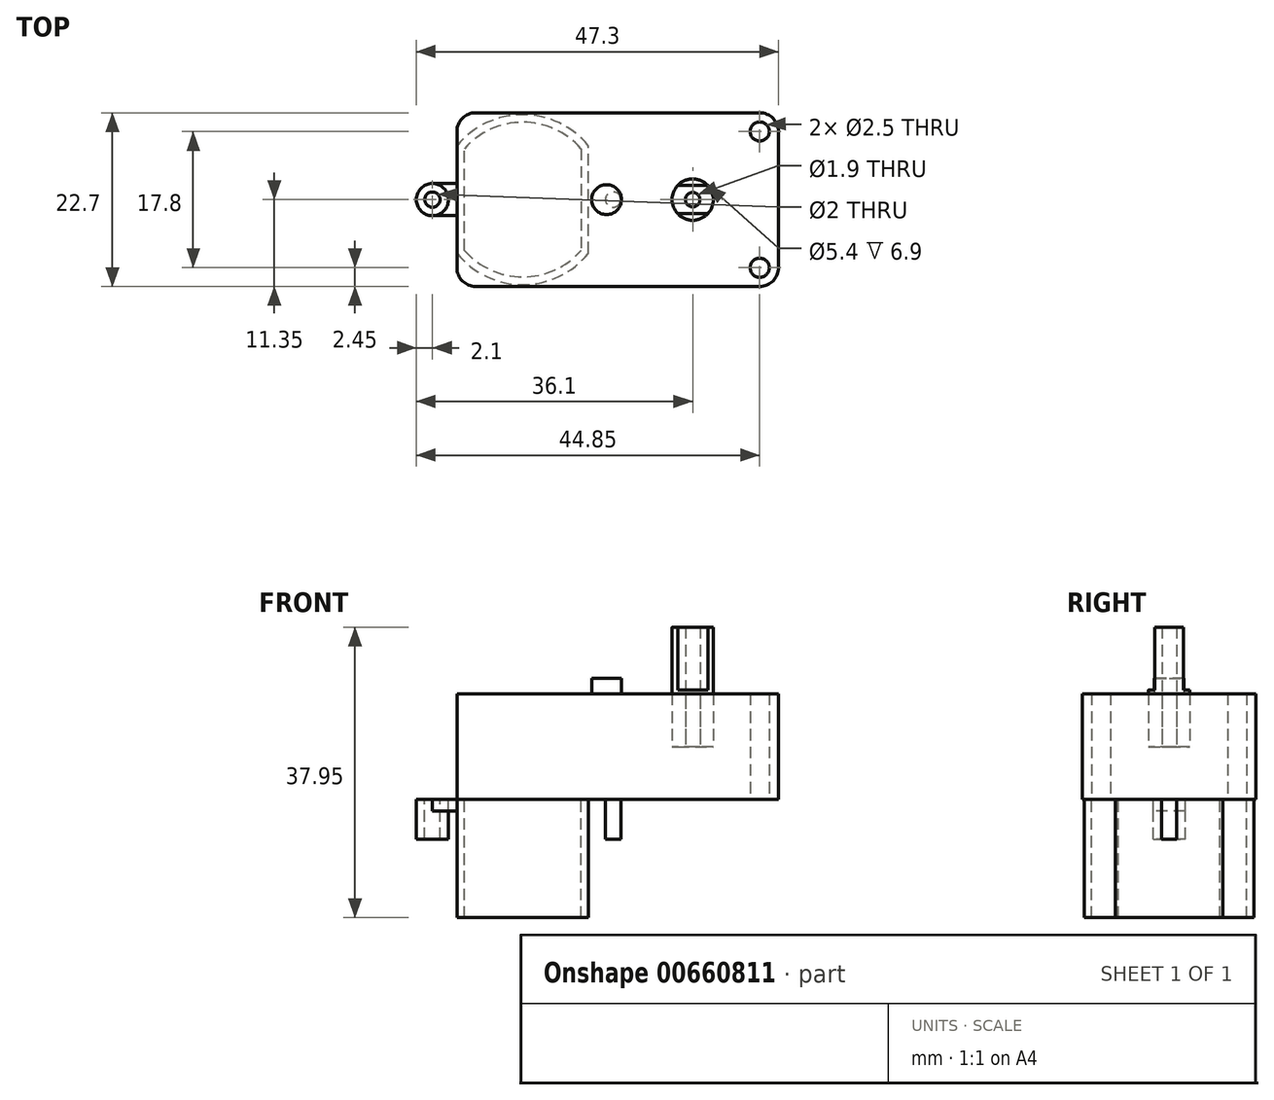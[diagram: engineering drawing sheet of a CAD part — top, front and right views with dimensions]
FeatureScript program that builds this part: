
annotation { "Feature Type Name" : "Feature", "Feature Type Description" : "" }
export const myFeature = defineFeature(function(context is Context, id is Id, definition is map)
    precondition{}
    {
        {
            var Q0;
            Q0=qCreatedBy(makeId("Top.planeOp"),FACE);
            var sketch = newSketch(context, id + "F0", { "sketchPlane" : qUnion([Q0])});
            skLineSegment(sketch, "E0.bottom", {"start": v(18.55, 11.35) * mm, "end": v(-18.55, 11.35) * mm});
            skLineSegment(sketch, "E0.top", {"start": v(18.55, -11.35) * mm, "end": v(-18.55, -11.35) * mm});
            skLineSegment(sketch, "E0.left", {"start": v(21, 8.9) * mm, "end": v(21, -8.9) * mm});
            skLineSegment(sketch, "E0.right", {"start": v(-21, 8.9) * mm, "end": v(-21, -8.9) * mm});
            skPoint(sketch, "E0.middle", {"position": v(0, 0) * mm});
            skLineSegment(sketch, "E1", {"start": v(-36.76, 0) * mm, "end": v(56.4, 0) * mm, "construction": true});
            skCircle(sketch, "E2", {"center": v(9.8, 0) * mm, "radius": 2.7 * mm});
            skPoint(sketch, "E3.visualSharp", {"position": v(21, 11.35) * mm});
            skArc(sketch, "E3.filletArc", {"start": v(21, 8.9) * mm, "mid": v(20.28, 10.63) * mm, "end": v(18.55, 11.35) * mm});
            skPoint(sketch, "E4.visualSharp", {"position": v(21, -11.35) * mm});
            skArc(sketch, "E4.filletArc", {"start": v(18.55, -11.35) * mm, "mid": v(20.28, -10.63) * mm, "end": v(21, -8.9) * mm});
            skPoint(sketch, "E5.visualSharp", {"position": v(-21, -11.35) * mm});
            skArc(sketch, "E5.filletArc", {"start": v(-21, -8.9) * mm, "mid": v(-20.28, -10.63) * mm, "end": v(-18.55, -11.35) * mm});
            skPoint(sketch, "E6.visualSharp", {"position": v(-21, 11.35) * mm});
            skArc(sketch, "E6.filletArc", {"start": v(-18.55, 11.35) * mm, "mid": v(-20.28, 10.63) * mm, "end": v(-21, 8.9) * mm});
            skCircle(sketch, "E7", {"center": v(18.55, 8.9) * mm, "radius": 1.25 * mm});
            skCircle(sketch, "E8", {"center": v(18.55, -8.9) * mm, "radius": 1.25 * mm});
            skCircle(sketch, "E9", {"center": v(9.8, 0) * mm, "radius": 0.95 * mm});
            skSolve(sketch);
        }
        {
            var Q0;
            Q0=makeQuery(id+"F0.imprint","IMPRINT",FACE,{"disambiguationData":[TD([[makeQuery(id+"F0.imprint","IMPRINT",EDGE,{"derivedFrom":sQuery(id+"F0.wireOp",EDGE,"E0.bottom")}),1.0]])]});
            extrude(context, id + "F1", {"entities" : qUnion([Q0]), "endBound" : BoundingType.SYMMETRIC, "depth" : 13.8 * mm, "offsetDistance" : 25 * mm});
        }
        {
            var Q0;
            Q0=makeQuery(id+"F0.imprint","IMPRINT",FACE,{"disambiguationData":[TD([[makeQuery(id+"F0.imprint","IMPRINT",EDGE,{"derivedFrom":sQuery(id+"F0.wireOp",EDGE,"E9")}),1.0]])]});
            extrude(context, id + "F2", {"entities" : qUnion([Q0]), "depth" : (13.8 / 2) * mm, "offsetDistance" : 25 * mm});
        }
        {
            var Q0;
            Q0=makeQuery(id+"F0.imprint","IMPRINT",FACE,{"disambiguationData":[TD([[makeQuery(id+"F0.imprint","IMPRINT",EDGE,{"derivedFrom":sQuery(id+"F0.wireOp",EDGE,"E2")}),1.0]])]});
            extrude(context, id + "F3", {"entities" : qUnion([Q0]), "depth" : (14.3 - 13.8 / 2) * mm, "offsetDistance" : 25 * mm});
        }
        {
            var Q0;
            Q0=makeQuery(id+"F3.opExtrude","CAP_FACE",FACE,{"disambiguationData":[OSD([sQuery(id+"F0.wireOp",EDGE,"E2"),sQuery(id+"F0.wireOp",EDGE,"E9")])],"isStart":false});
            var sketch = newSketch(context, id + "F4", { "sketchPlane" : qUnion([Q0])});
            skCircle(sketch, "E10.0.0", {"center": v(9.8, 0) * mm, "radius": 2.7 * mm});
            skLineSegment(sketch, "E11.bottom", {"start": v(11.77, 1.85) * mm, "end": v(7.83, 1.85) * mm});
            skLineSegment(sketch, "E11.top", {"start": v(11.77, -1.85) * mm, "end": v(7.83, -1.85) * mm});
            skPoint(sketch, "E11.right.end.orphan", {"position": v(5.74, -1.85) * mm});
            skPoint(sketch, "E12.orphan", {"position": v(5.62, 1.85) * mm});
            skPoint(sketch, "E13.orphan", {"position": v(13.86, 1.85) * mm});
            skPoint(sketch, "E14.orphan", {"position": v(13.98, -1.85) * mm});
            skSolve(sketch);
        }
        {
            var Q0;
            {var subQ1=sQuery(id+"F4.wireOp",EDGE,"E11.bottom");Q0=makeQuery(id+"F4.imprint","IMPRINT",FACE,{"disambiguationData":[TD([[makeQuery(id+"F4.imprint","IMPRINT",EDGE,{"derivedFrom":subQ1}),1.0]])]});}
            extrude(context, id + "F5", {"entities" : qUnion([Q0]), "operationType" : NewBodyOperationType.ADD, "depth" : 8.2 * mm, "offsetDistance" : 25 * mm});
        }
        {
            var Q0;
            Q0=makeQuery(id+"F0.imprint","IMPRINT",FACE,{"disambiguationData":[TD([[makeQuery(id+"F0.imprint","IMPRINT",EDGE,{"derivedFrom":sQuery(id+"F0.wireOp",EDGE,"E2")}),1.0]])]});
            var Q1;
            Q1=makeQuery(id+"F0.imprint","IMPRINT",FACE,{"disambiguationData":[TD([[makeQuery(id+"F0.imprint","IMPRINT",EDGE,{"derivedFrom":sQuery(id+"F0.wireOp",EDGE,"E9")}),1.0]])]});
            var Q2;
            Q2=makeQuery(id+"F1.opExtrude","CAP_FACE",FACE,{"disambiguationData":[OSD([sQuery(id+"F0.wireOp",EDGE,"E0.bottom"),sQuery(id+"F0.wireOp",EDGE,"E0.top"),sQuery(id+"F0.wireOp",EDGE,"E0.left"),sQuery(id+"F0.wireOp",EDGE,"E0.right"),sQuery(id+"F0.wireOp",EDGE,"E2"),sQuery(id+"F0.wireOp",EDGE,"E3.filletArc"),sQuery(id+"F0.wireOp",EDGE,"E4.filletArc"),sQuery(id+"F0.wireOp",EDGE,"E5.filletArc"),sQuery(id+"F0.wireOp",EDGE,"E6.filletArc"),sQuery(id+"F0.wireOp",EDGE,"E7"),sQuery(id+"F0.wireOp",EDGE,"E8")])],"isStart":true});
            extrude(context, id + "F6", {"entities" : qUnion([Q0, Q1]), "endBound" : BoundingType.UP_TO_SURFACE, "oppositeDirection" : true, "depth" : 25 * mm, "endBoundEntityFace" : qUnion([Q2]), "offsetDistance" : 25 * mm});
        }
        {
            var Q0;
            Q0=makeQuery(id+"F6.opExtrude","SWEPT_BODY",BODY,{"disambiguationData":[OSD([sQuery(id+"F0.wireOp",EDGE,"E2")])]});
            var Q1;
            Q1=makeQuery(id+"F1.opExtrude","SWEPT_BODY",BODY,{"disambiguationData":[OSD([sQuery(id+"F0.wireOp",EDGE,"E0.bottom"),sQuery(id+"F0.wireOp",EDGE,"E0.top"),sQuery(id+"F0.wireOp",EDGE,"E0.left"),sQuery(id+"F0.wireOp",EDGE,"E0.right"),sQuery(id+"F0.wireOp",EDGE,"E2"),sQuery(id+"F0.wireOp",EDGE,"E3.filletArc"),sQuery(id+"F0.wireOp",EDGE,"E4.filletArc"),sQuery(id+"F0.wireOp",EDGE,"E5.filletArc"),sQuery(id+"F0.wireOp",EDGE,"E6.filletArc"),sQuery(id+"F0.wireOp",EDGE,"E7"),sQuery(id+"F0.wireOp",EDGE,"E8")])]});
            booleanBodies(context, id + "F7", {"operationType" : BooleanOperationType.UNION, "tools" : qUnion([Q0, Q1])});
        }
        {
            var Q0;
            {var subQ0=sQuery(id+"F0.wireOp",EDGE,"E8");var subQ1=sQuery(id+"F0.wireOp",EDGE,"E7");var subQ2=sQuery(id+"F0.wireOp",EDGE,"E6.filletArc");var subQ3=sQuery(id+"F0.wireOp",EDGE,"E5.filletArc");var subQ4=sQuery(id+"F0.wireOp",EDGE,"E4.filletArc");var subQ5=sQuery(id+"F0.wireOp",EDGE,"E3.filletArc");var subQ6=sQuery(id+"F0.wireOp",EDGE,"E2");var subQ7=sQuery(id+"F0.wireOp",EDGE,"E0.right");var subQ8=sQuery(id+"F0.wireOp",EDGE,"E0.left");var subQ9=sQuery(id+"F0.wireOp",EDGE,"E0.top");var subQ10=sQuery(id+"F0.wireOp",EDGE,"E0.bottom");Q0=makeQuery(id+"F7.opBoolean","MERGE",FACE,{"derivedFrom":[makeQuery(id+"F1.opExtrude","CAP_FACE",FACE,{"disambiguationData":[OSD([subQ10,subQ9,subQ8,subQ7,subQ6,subQ5,subQ4,subQ3,subQ2,subQ1,subQ0])],"isStart":true}),makeQuery(id+"F6.opExtrude","CAP_FACE",FACE,{"disambiguationData":[OSD([subQ10,subQ9,subQ8,subQ7,subQ6,subQ5,subQ4,subQ3,subQ2,subQ1,subQ0])],"isStart":false})]});}
            var sketch = newSketch(context, id + "F8", { "sketchPlane" : qUnion([Q0])});
            skLineSegment(sketch, "E15.0.0", {"start": v(18.55, 11.35) * mm, "end": v(-18.55, 11.35) * mm});
            skArc(sketch, "E15.0.1", {"start": v(-18.55, 11.35) * mm, "mid": v(-20.28, 10.63) * mm, "end": v(-21, 8.9) * mm});
            skLineSegment(sketch, "E15.0.2", {"start": v(-21, 7.02) * mm, "end": v(-21, -7.02) * mm});
            skArc(sketch, "E15.0.3", {"start": v(-21, -8.9) * mm, "mid": v(-20.28, -10.63) * mm, "end": v(-18.55, -11.35) * mm});
            skLineSegment(sketch, "E15.0.4", {"start": v(-18.55, -11.35) * mm, "end": v(18.55, -11.35) * mm});
            skArc(sketch, "E15.0.5", {"start": v(18.55, -11.35) * mm, "mid": v(20.28, -10.63) * mm, "end": v(21, -8.9) * mm});
            skLineSegment(sketch, "E15.0.6", {"start": v(21, -8.9) * mm, "end": v(21, 8.9) * mm});
            skArc(sketch, "E15.0.7", {"start": v(21, 8.9) * mm, "mid": v(20.28, 10.63) * mm, "end": v(18.55, 11.35) * mm});
            skArc(sketch, "E16", {"start": v(-21, -7.02) * mm, "mid": v(-12.4, -11.1) * mm, "end": v(-3.8, -7.02) * mm});
            skPoint(sketch, "E16.centerSnap0", {"position": v(-21, 0) * mm});
            skLineSegment(sketch, "E17", {"start": v(-21, 7.02) * mm, "end": v(-1.14, 7.02) * mm, "construction": true});
            skLineSegment(sketch, "E18", {"start": v(-21, -7.02) * mm, "end": v(-0.71, -7.02) * mm, "construction": true});
            skLineSegment(sketch, "E19", {"start": v(-3.8, -7.02) * mm, "end": v(-3.8, 7.02) * mm, "construction": true});
            skArc(sketch, "E20.trimOffspring", {"start": v(-3.8, 7.02) * mm, "mid": v(-12.4, 11.1) * mm, "end": v(-21, 7.02) * mm});
            skLineSegment(sketch, "E21", {"start": v(-3.8, 7.02) * mm, "end": v(-3.8, -7.02) * mm});
            skArc(sketch, "E22.0", {"start": v(-4.8, 6.65) * mm, "mid": v(-12.4, 10.1) * mm, "end": v(-20, 6.65) * mm});
            skLineSegment(sketch, "E22.1", {"start": v(-4.8, -6.65) * mm, "end": v(-4.8, 6.65) * mm});
            skArc(sketch, "E22.2", {"start": v(-20, -6.65) * mm, "mid": v(-12.4, -10.1) * mm, "end": v(-4.8, -6.65) * mm});
            skLineSegment(sketch, "E22.3", {"start": v(-20, 6.65) * mm, "end": v(-20, -6.65) * mm});
            skLineSegment(sketch, "E23", {"start": v(-21, 2.1) * mm, "end": v(-26.3, 2.1) * mm});
            skLineSegment(sketch, "E24", {"start": v(-26.3, 2.1) * mm, "end": v(-26.3, 0) * mm});
            skLineSegment(sketch, "E25.MirrorCS", {"start": v(-21, -2.1) * mm, "end": v(-26.3, -2.1) * mm});
            skLineSegment(sketch, "E26.MirrorCS", {"start": v(-26.3, -2.1) * mm, "end": v(-26.3, 0) * mm});
            skLineSegment(sketch, "E27", {"start": v(-12.4, 0) * mm, "end": v(-12.4, 13.38) * mm, "construction": true});
            skLineSegment(sketch, "E28.MirrorCS", {"start": v(-3.8, 2.1) * mm, "end": v(1.5, 2.1) * mm});
            skLineSegment(sketch, "E29.MirrorCS", {"start": v(-3.8, -2.1) * mm, "end": v(1.5, -2.1) * mm});
            skLineSegment(sketch, "E30.MirrorCS", {"start": v(1.5, -2.1) * mm, "end": v(1.5, 0) * mm});
            skLineSegment(sketch, "E31.MirrorCS", {"start": v(1.5, 2.1) * mm, "end": v(1.5, 0) * mm});
            skCircle(sketch, "E32", {"center": v(-24.2, 0) * mm, "radius": 2.1 * mm});
            skCircle(sketch, "E33", {"center": v(-24.2, 0) * mm, "radius": 1 * mm});
            skCircle(sketch, "E34.MirrorC", {"center": v(-0.6, 0) * mm, "radius": 2.1 * mm});
            skCircle(sketch, "E35.MirrorC", {"center": v(-0.6, 0) * mm, "radius": 1 * mm});
            skSolve(sketch);
        }
        {
            var Q0;
            {var subQ4=sQuery(id+"F8.wireOp",EDGE,"E16");Q0=makeQuery(id+"F8.imprint","IMPRINT",FACE,{"disambiguationData":[TD([[makeQuery(id+"F8.imprint","IMPRINT",EDGE,{"derivedFrom":subQ4}),1.0]])]});}
            extrude(context, id + "F9", {"entities" : qUnion([Q0]), "operationType" : NewBodyOperationType.ADD, "depth" : 15.45 * mm, "offsetDistance" : 25 * mm});
        }
        {
            var Q0;
            {var subQ0=sQuery(id+"F8.wireOp",EDGE,"E23");var subQ1=sQuery(id+"F8.wireOp",EDGE,"E15.0.2");var subQ2=makeQuery(id+"F8.imprint","INTERSECT",VERTEX,{"derivedFrom":[subQ1,subQ0]});Q0=makeQuery(id+"F8.imprint","IMPRINT",FACE,{"disambiguationData":[TD([[makeQuery(id+"F8.imprint","IMPRINT",EDGE,{"disambiguationData":[TD([[subQ2,1.0]])],"derivedFrom":subQ1}),1.0]])]});}
            extrude(context, id + "F10", {"entities" : qUnion([Q0]), "operationType" : NewBodyOperationType.ADD, "depth" : 1.5 * mm, "offsetDistance" : 25 * mm});
        }
        {
            var Q0;
            Q0=makeQuery(id+"F8.imprint","IMPRINT",FACE,{"disambiguationData":[TD([[makeQuery(id+"F8.imprint","IMPRINT",EDGE,{"derivedFrom":sQuery(id+"F8.wireOp",EDGE,"E33")}),-1.0]])]});
            var Q1;
            Q1=makeQuery(id+"F8.imprint","IMPRINT",FACE,{"disambiguationData":[TD([[makeQuery(id+"F8.imprint","IMPRINT",EDGE,{"derivedFrom":sQuery(id+"F8.wireOp",EDGE,"E35.MirrorC")}),1.0]])]});
            extrude(context, id + "F11", {"entities" : qUnion([Q0, Q1]), "depth" : 5.2 * mm, "offsetDistance" : 25 * mm});
        }
        {
            var Q0;
            Q0=makeQuery(id+"F1.opExtrude","CAP_FACE",FACE,{"disambiguationData":[OSD([sQuery(id+"F0.wireOp",EDGE,"E0.bottom"),sQuery(id+"F0.wireOp",EDGE,"E0.top"),sQuery(id+"F0.wireOp",EDGE,"E0.left"),sQuery(id+"F0.wireOp",EDGE,"E0.right"),sQuery(id+"F0.wireOp",EDGE,"E2"),sQuery(id+"F0.wireOp",EDGE,"E3.filletArc"),sQuery(id+"F0.wireOp",EDGE,"E4.filletArc"),sQuery(id+"F0.wireOp",EDGE,"E5.filletArc"),sQuery(id+"F0.wireOp",EDGE,"E6.filletArc"),sQuery(id+"F0.wireOp",EDGE,"E7"),sQuery(id+"F0.wireOp",EDGE,"E8")])],"isStart":false});
            var sketch = newSketch(context, id + "F12", { "sketchPlane" : qUnion([Q0])});
            skCircle(sketch, "E36", {"center": v(-1.45, 0) * mm, "radius": 1.95 * mm});
            skSolve(sketch);
        }
        {
            var Q0;
            Q0=makeQuery(id+"F12.imprint","IMPRINT",FACE,{"disambiguationData":[TD([[makeQuery(id+"F12.imprint","IMPRINT",EDGE,{"derivedFrom":sQuery(id+"F12.wireOp",EDGE,"E36")}),1.0]])]});
            extrude(context, id + "F13", {"entities" : qUnion([Q0]), "operationType" : NewBodyOperationType.ADD, "depth" : 2 * mm, "offsetDistance" : 25 * mm});
        }
    });
